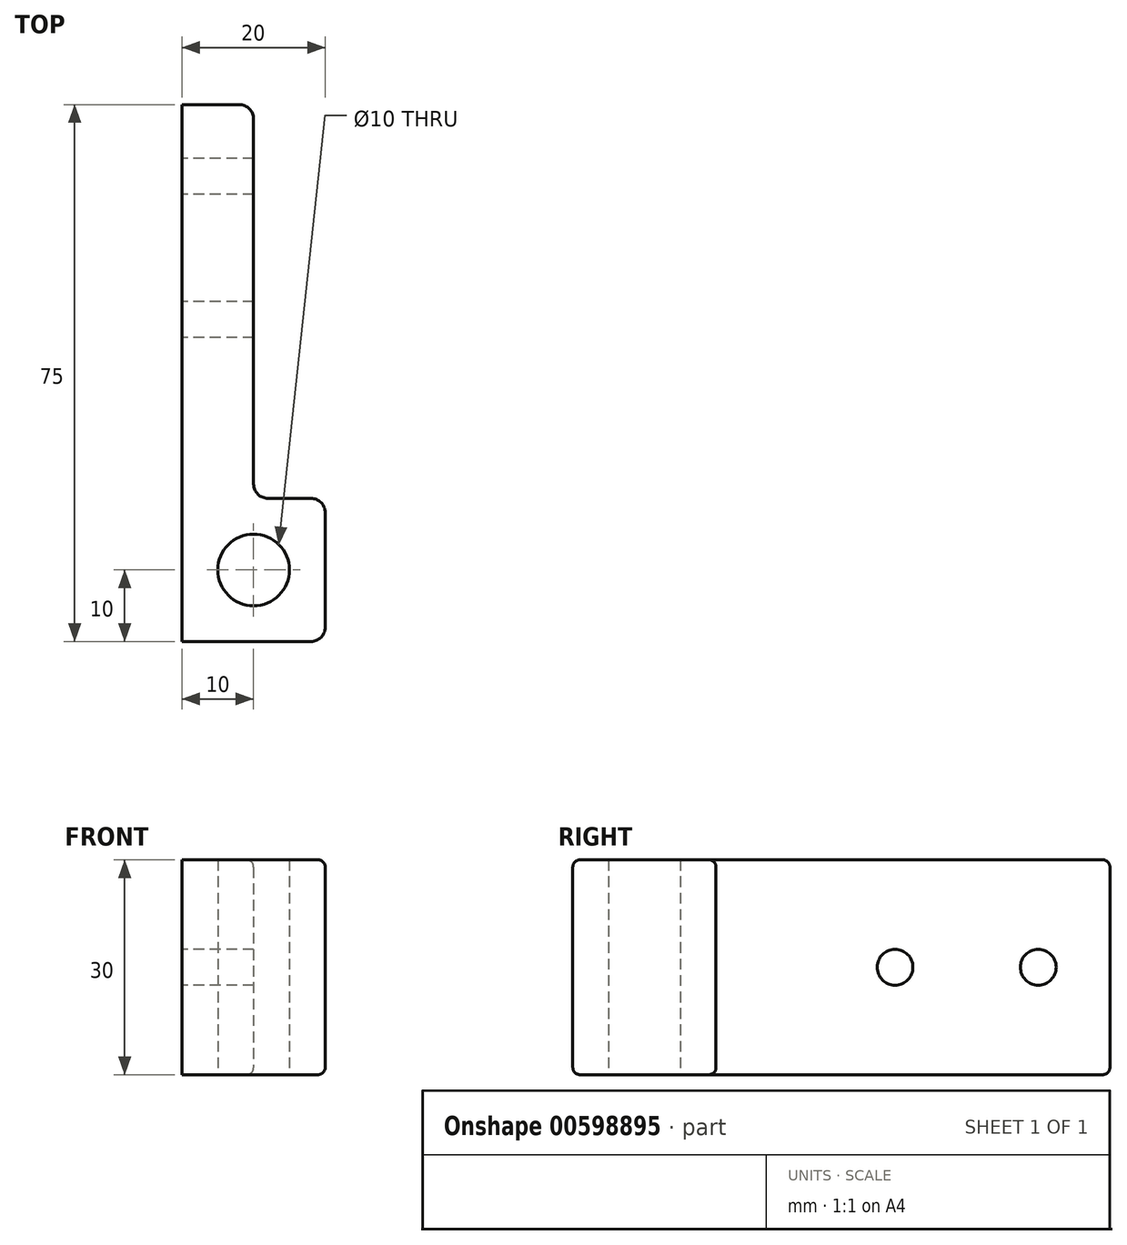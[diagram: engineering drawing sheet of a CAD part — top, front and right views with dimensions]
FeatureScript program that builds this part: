
annotation { "Feature Type Name" : "Feature", "Feature Type Description" : "" }
export const myFeature = defineFeature(function(context is Context, id is Id, definition is map)
    precondition{}
    {
        {
            var Q0;
            Q0=qCreatedBy(makeId("Top.planeOp"),FACE);
            var sketch = newSketch(context, id + "F0", { "sketchPlane" : qUnion([Q0])});
            skLineSegment(sketch, "E0", {"start": v(0, 0) * mm, "end": v(0, -75) * mm});
            skLineSegment(sketch, "E1", {"start": v(0, -75) * mm, "end": v(20, -75) * mm});
            skLineSegment(sketch, "E2", {"start": v(20, -75) * mm, "end": v(20, -55) * mm});
            skLineSegment(sketch, "E3", {"start": v(20, -55) * mm, "end": v(10, -55) * mm});
            skLineSegment(sketch, "E4", {"start": v(10, -55) * mm, "end": v(10, 0) * mm});
            skLineSegment(sketch, "E5", {"start": v(10, 0) * mm, "end": v(0, 0) * mm});
            skSolve(sketch);
        }
        {
            var Q0;
            Q0=qSketchRegion(id+"F0",true);
            extrude(context, id + "F1", {"entities" : qUnion([Q0]), "depth" : 30 * mm, "offsetDistance" : 25 * mm});
        }
        {
            var Q0;
            Q0=makeQuery(id+"F1.opExtrude","CAP_FACE",FACE,{"disambiguationData":[OSD([sQuery(id+"F0.wireOp",EDGE,"E0"),sQuery(id+"F0.wireOp",EDGE,"E1"),sQuery(id+"F0.wireOp",EDGE,"E2"),sQuery(id+"F0.wireOp",EDGE,"E3"),sQuery(id+"F0.wireOp",EDGE,"E4"),sQuery(id+"F0.wireOp",EDGE,"E5")])],"isStart":false});
            var sketch = newSketch(context, id + "F2", { "sketchPlane" : qUnion([Q0])});
            skLineSegment(sketch, "E6", {"start": v(20, -65) * mm, "end": v(0, -65) * mm});
            skPoint(sketch, "E7", {"position": v(10, -65) * mm});
            skSolve(sketch);
        }
        {
            var Q0;
            Q0=sQuery(id+"F2.wireOp",VERTEX,"E7");
            var Q1;
            Q1=makeQuery(id+"F1.opExtrude","SWEPT_BODY",BODY,{"disambiguationData":[OSD([sQuery(id+"F0.wireOp",EDGE,"E0"),sQuery(id+"F0.wireOp",EDGE,"E1"),sQuery(id+"F0.wireOp",EDGE,"E2"),sQuery(id+"F0.wireOp",EDGE,"E3"),sQuery(id+"F0.wireOp",EDGE,"E4"),sQuery(id+"F0.wireOp",EDGE,"E5")])]});
            hole(context, id + "F3", {"style" : HoleStyle.SIMPLE, "endStyle" : HoleEndStyle.THROUGH, "holeDiameter" : 10 * mm, "majorDiameter" : 5 * mm, "isTappedThrough" : true, "tappedDepth" : 12 * mm, "tapClearance" : 3, "locations" : qUnion([Q0]), "scope" : qUnion([Q1])});
        }
        {
            var Q0;
            Q0=makeQuery(id+"F1.opExtrude","SWEPT_FACE",FACE,{"disambiguationData":[OSD([sQuery(id+"F0.wireOp",EDGE,"E4")])]});
            var sketch = newSketch(context, id + "F4", { "sketchPlane" : qUnion([Q0])});
            skLineSegment(sketch, "E8", {"start": v(0, 15) * mm, "end": v(-26.63, 15) * mm});
            skPoint(sketch, "E9", {"position": v(-10, 15) * mm});
            skSolve(sketch);
        }
        {
            var Q0;
            Q0=sQuery(id+"F4.wireOp",VERTEX,"E9");
            var Q1;
            Q1=makeQuery(id+"F1.opExtrude","SWEPT_BODY",BODY,{"disambiguationData":[OSD([sQuery(id+"F0.wireOp",EDGE,"E0"),sQuery(id+"F0.wireOp",EDGE,"E1"),sQuery(id+"F0.wireOp",EDGE,"E2"),sQuery(id+"F0.wireOp",EDGE,"E3"),sQuery(id+"F0.wireOp",EDGE,"E4"),sQuery(id+"F0.wireOp",EDGE,"E5")])]});
            hole(context, id + "F5", {"style" : HoleStyle.SIMPLE, "endStyle" : HoleEndStyle.THROUGH, "holeDiameter" : 5 * mm, "majorDiameter" : 5 * mm, "isTappedThrough" : true, "tappedDepth" : 12 * mm, "tapClearance" : 3, "locations" : qUnion([Q0]), "scope" : qUnion([Q1])});
        }
        {
            var Q0;
            Q0=makeQuery(id+"F1.opExtrude","SWEPT_FACE",FACE,{"disambiguationData":[OSD([sQuery(id+"F0.wireOp",EDGE,"E4")])]});
            var sketch = newSketch(context, id + "F6", { "sketchPlane" : qUnion([Q0])});
            skLineSegment(sketch, "E10", {"start": v(0, 15) * mm, "end": v(-28.1, 15) * mm});
            skPoint(sketch, "E11", {"position": v(-30, 15) * mm});
            skSolve(sketch);
        }
        {
            var Q0;
            Q0=sQuery(id+"F6.wireOp",VERTEX,"E11");
            var Q1;
            Q1=makeQuery(id+"F1.opExtrude","SWEPT_BODY",BODY,{"disambiguationData":[OSD([sQuery(id+"F0.wireOp",EDGE,"E0"),sQuery(id+"F0.wireOp",EDGE,"E1"),sQuery(id+"F0.wireOp",EDGE,"E2"),sQuery(id+"F0.wireOp",EDGE,"E3"),sQuery(id+"F0.wireOp",EDGE,"E4"),sQuery(id+"F0.wireOp",EDGE,"E5")])]});
            hole(context, id + "F7", {"style" : HoleStyle.SIMPLE, "endStyle" : HoleEndStyle.THROUGH, "holeDiameter" : 5 * mm, "majorDiameter" : 5 * mm, "isTappedThrough" : true, "tappedDepth" : 12 * mm, "tapClearance" : 3, "locations" : qUnion([Q0]), "scope" : qUnion([Q1])});
        }
        {
            var Q0;
            Q0=makeQuery(id+"F1.opExtrude","SWEPT_EDGE",EDGE,{"disambiguationData":[OSD([sQuery(id+"F0.wireOp",EDGE,"E4"),sQuery(id+"F0.wireOp",EDGE,"E5")])]});
            var Q1;
            Q1=makeQuery(id+"F1.opExtrude","SWEPT_EDGE",EDGE,{"disambiguationData":[OSD([sQuery(id+"F0.wireOp",EDGE,"E2"),sQuery(id+"F0.wireOp",EDGE,"E3")])]});
            var Q2;
            Q2=makeQuery(id+"F1.opExtrude","SWEPT_EDGE",EDGE,{"disambiguationData":[OSD([sQuery(id+"F0.wireOp",EDGE,"E3"),sQuery(id+"F0.wireOp",EDGE,"E4")])]});
            var Q3;
            Q3=makeQuery(id+"F1.opExtrude","SWEPT_EDGE",EDGE,{"disambiguationData":[OSD([sQuery(id+"F0.wireOp",EDGE,"E1"),sQuery(id+"F0.wireOp",EDGE,"E2")])]});
            fillet(context, id + "F8", {"entities" : qUnion([Q0, Q1, Q2, Q3]), "radius" : 2 * mm, "tangentPropagation" : true, "allowEdgeOverflow" : false});
        }
        {
            var Q0;
            Q0=makeQuery(id+"F1.opExtrude","CAP_EDGE",EDGE,{"disambiguationData":[OSD([sQuery(id+"F0.wireOp",EDGE,"E5")])],"isStart":false});
            var Q1;
            Q1=makeQuery(id+"F1.opExtrude","CAP_EDGE",EDGE,{"disambiguationData":[OSD([sQuery(id+"F0.wireOp",EDGE,"E4")])],"isStart":true});
            fillet(context, id + "F9", {"entities" : qUnion([Q0, Q1]), "radius" : 1 * mm, "tangentPropagation" : true, "allowEdgeOverflow" : false});
        }
    });
